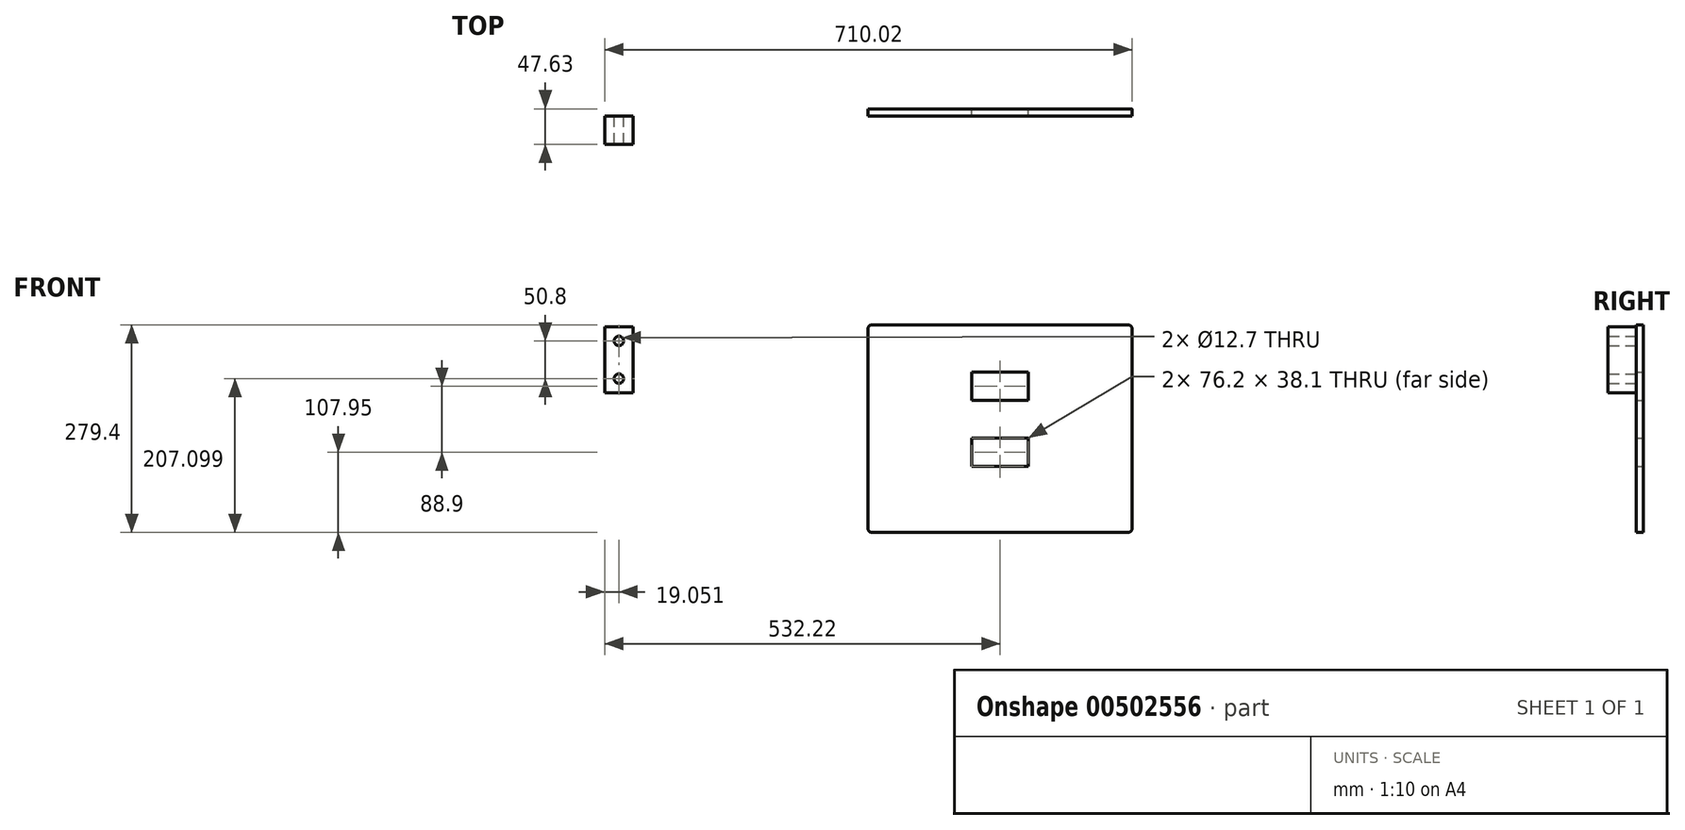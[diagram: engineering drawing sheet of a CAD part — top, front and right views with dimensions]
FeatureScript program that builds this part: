
annotation { "Feature Type Name" : "Feature", "Feature Type Description" : "" }
export const myFeature = defineFeature(function(context is Context, id is Id, definition is map)
    precondition{}
    {
        {
            var Q0;
            Q0=qCreatedBy(makeId("Front.planeOp"),FACE);
            var sketch = newSketch(context, id + "F0", { "sketchPlane" : qUnion([Q0])});
            skLineSegment(sketch, "E0.bottom", {"start": v(177.8, -139.7) * mm, "end": v(-177.8, -139.7) * mm});
            skLineSegment(sketch, "E0.top", {"start": v(177.8, 139.7) * mm, "end": v(-177.8, 139.7) * mm});
            skLineSegment(sketch, "E0.left", {"start": v(177.8, -139.7) * mm, "end": v(177.8, 139.7) * mm});
            skLineSegment(sketch, "E0.right", {"start": v(-177.8, -139.7) * mm, "end": v(-177.8, 139.7) * mm});
            skPoint(sketch, "E0.middle", {"position": v(0, 0) * mm});
            skLineSegment(sketch, "E1", {"start": v(0, 76.2) * mm, "end": v(38.1, 76.2) * mm});
            skLineSegment(sketch, "E2", {"start": v(38.1, 76.2) * mm, "end": v(38.1, 38.1) * mm});
            skLineSegment(sketch, "E3", {"start": v(38.1, 38.1) * mm, "end": v(-38.1, 38.1) * mm});
            skLineSegment(sketch, "E4", {"start": v(-38.1, 38.1) * mm, "end": v(-38.1, 76.2) * mm});
            skLineSegment(sketch, "E5", {"start": v(-38.1, 76.2) * mm, "end": v(0, 76.2) * mm});
            skLineSegment(sketch, "E6", {"start": v(0, -12.7) * mm, "end": v(38.1, -12.7) * mm});
            skLineSegment(sketch, "E7", {"start": v(38.1, -12.7) * mm, "end": v(38.1, -50.8) * mm});
            skLineSegment(sketch, "E8", {"start": v(38.1, -50.8) * mm, "end": v(-38.1, -50.8) * mm});
            skLineSegment(sketch, "E9", {"start": v(-38.1, -50.8) * mm, "end": v(-38.1, -12.7) * mm});
            skLineSegment(sketch, "E10", {"start": v(-38.1, -12.7) * mm, "end": v(0, -12.7) * mm});
            skLineSegment(sketch, "E11", {"start": v(0, 76.2) * mm, "end": v(0, 139.7) * mm});
            skLineSegment(sketch, "E12", {"start": v(0, 38.1) * mm, "end": v(0, -12.7) * mm});
            skSolve(sketch);
        }
        {
            var Q0;
            Q0=makeQuery(id+"F0.imprint","IMPRINT",FACE,{"disambiguationData":[TD([[makeQuery(id+"F0.imprint","IMPRINT",EDGE,{"derivedFrom":sQuery(id+"F0.wireOp",EDGE,"E0.bottom")}),-1.0]])]});
            extrude(context, id + "F1", {"entities" : qUnion([Q0]), "depth" : 9.52 * mm, "offsetDistance" : 25.4 * mm});
        }
        {
            var Q0;
            Q0=makeQuery(id+"F1.opExtrude","SWEPT_EDGE",EDGE,{"disambiguationData":[OSD([sQuery(id+"F0.wireOp",EDGE,"E0.top"),sQuery(id+"F0.wireOp",EDGE,"E0.right")])]});
            var Q1;
            Q1=makeQuery(id+"F1.opExtrude","SWEPT_EDGE",EDGE,{"disambiguationData":[OSD([sQuery(id+"F0.wireOp",EDGE,"E0.top"),sQuery(id+"F0.wireOp",EDGE,"E0.left")])]});
            var Q2;
            Q2=makeQuery(id+"F1.opExtrude","SWEPT_EDGE",EDGE,{"disambiguationData":[OSD([sQuery(id+"F0.wireOp",EDGE,"E0.bottom"),sQuery(id+"F0.wireOp",EDGE,"E0.left")])]});
            var Q3;
            Q3=makeQuery(id+"F1.opExtrude","SWEPT_EDGE",EDGE,{"disambiguationData":[OSD([sQuery(id+"F0.wireOp",EDGE,"E0.bottom"),sQuery(id+"F0.wireOp",EDGE,"E0.right")])]});
            fillet(context, id + "F2", {"entities" : qUnion([Q0, Q1, Q2, Q3]), "radius" : 5.08 * mm, "tangentPropagation" : true, "allowEdgeOverflow" : false});
        }
        {
            var Q0;
            Q0=makeQuery(id+"F1.opExtrude","CAP_FACE",FACE,{"disambiguationData":[OSD([sQuery(id+"F0.wireOp",EDGE,"E0.bottom"),sQuery(id+"F0.wireOp",EDGE,"E0.top"),sQuery(id+"F0.wireOp",EDGE,"E0.left"),sQuery(id+"F0.wireOp",EDGE,"E0.right"),sQuery(id+"F0.wireOp",EDGE,"E1"),sQuery(id+"F0.wireOp",EDGE,"E2"),sQuery(id+"F0.wireOp",EDGE,"E3"),sQuery(id+"F0.wireOp",EDGE,"E4"),sQuery(id+"F0.wireOp",EDGE,"E5"),sQuery(id+"F0.wireOp",EDGE,"E6"),sQuery(id+"F0.wireOp",EDGE,"E7"),sQuery(id+"F0.wireOp",EDGE,"E8"),sQuery(id+"F0.wireOp",EDGE,"E9"),sQuery(id+"F0.wireOp",EDGE,"E10")])],"isStart":false});
            var sketch = newSketch(context, id + "F3", { "sketchPlane" : qUnion([Q0])});
            skLineSegment(sketch, "E13.bottom", {"start": v(-494.12, 48.35) * mm, "end": v(-532.22, 48.35) * mm});
            skLineSegment(sketch, "E13.top", {"start": v(-494.12, 137.25) * mm, "end": v(-532.22, 137.25) * mm});
            skLineSegment(sketch, "E13.left", {"start": v(-494.12, 48.35) * mm, "end": v(-494.12, 137.25) * mm});
            skLineSegment(sketch, "E13.right", {"start": v(-532.22, 48.35) * mm, "end": v(-532.22, 137.25) * mm});
            skPoint(sketch, "E13.middle", {"position": v(-513.17, 92.8) * mm});
            skCircle(sketch, "E14", {"center": v(-513.17, 67.4) * mm, "radius": 6.35 * mm});
            skCircle(sketch, "E15", {"center": v(-513.17, 118.2) * mm, "radius": 6.35 * mm});
            skSolve(sketch);
        }
        {
            var Q0;
            Q0=makeQuery(id+"F3.imprint","IMPRINT",FACE,{"disambiguationData":[TD([[makeQuery(id+"F3.imprint","IMPRINT",EDGE,{"derivedFrom":sQuery(id+"F3.wireOp",EDGE,"E13.bottom")}),-1.0]])]});
            extrude(context, id + "F4", {"entities" : qUnion([Q0]), "depth" : 38.1 * mm, "offsetDistance" : 25.4 * mm});
        }
    });
